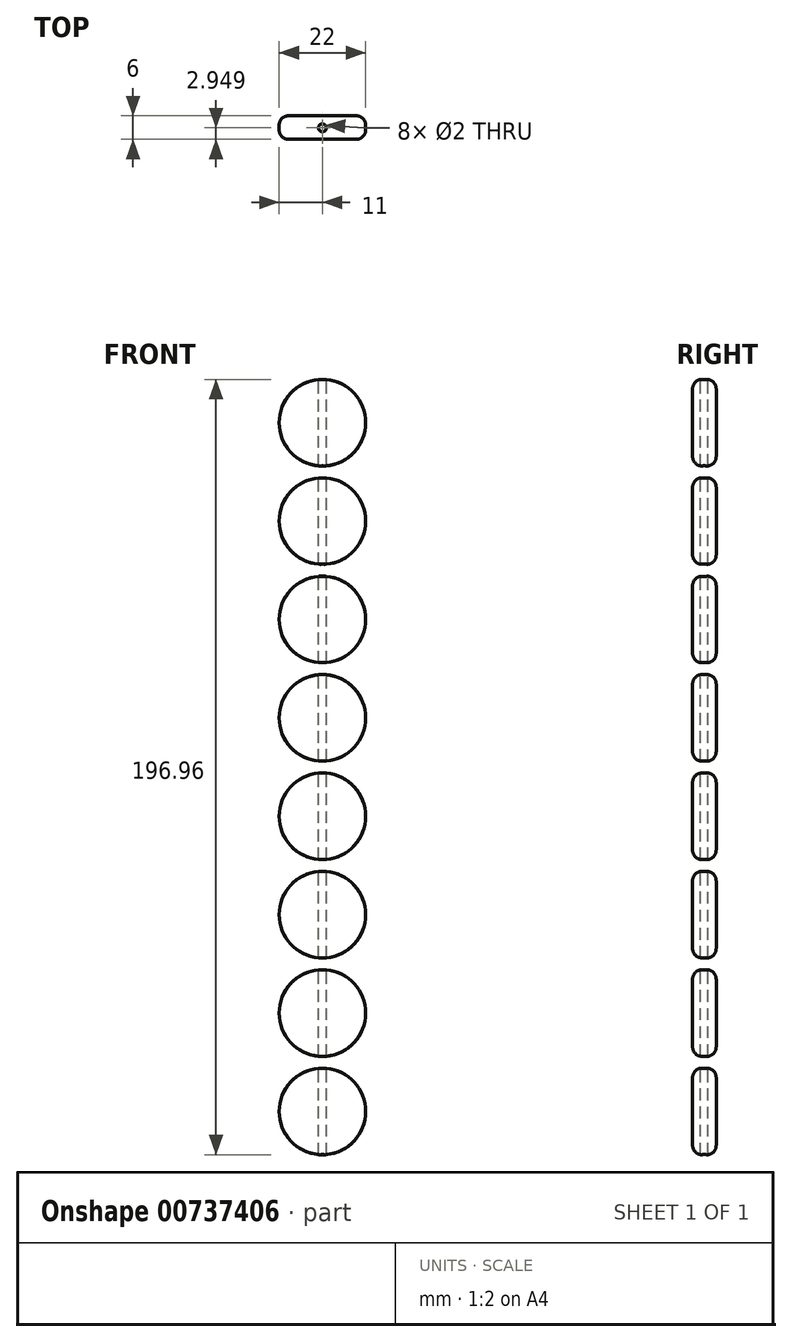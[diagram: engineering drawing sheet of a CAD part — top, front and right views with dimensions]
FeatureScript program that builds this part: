
annotation { "Feature Type Name" : "Feature", "Feature Type Description" : "" }
export const myFeature = defineFeature(function(context is Context, id is Id, definition is map)
    precondition{}
    {
        {
            var Q0;
            Q0=qCreatedBy(makeId("Front.planeOp"),FACE);
            var sketch = newSketch(context, id + "F0", { "sketchPlane" : qUnion([Q0])});
            skCircle(sketch, "E0", {"center": v(0, 0) * mm, "radius": 11 * mm});
            skCircle(sketch, "E1.0.1.0", {"center": v(0, -25) * mm, "radius": 11 * mm});
            skCircle(sketch, "E1.0.2.0", {"center": v(0, -50) * mm, "radius": 11 * mm});
            skCircle(sketch, "E1.0.3.0", {"center": v(0, -75) * mm, "radius": 11 * mm});
            skCircle(sketch, "E1.0.4.0", {"center": v(0, -100) * mm, "radius": 11 * mm});
            skCircle(sketch, "E1.0.5.0", {"center": v(0, -125) * mm, "radius": 11 * mm});
            skCircle(sketch, "E1.0.6.0", {"center": v(0, -150) * mm, "radius": 11 * mm});
            skCircle(sketch, "E1.0.7.0", {"center": v(0, -175) * mm, "radius": 11 * mm});
            skLineSegment(sketch, "E1.direction1", {"start": v(0, 0) * mm, "end": v(25, 0) * mm, "construction": true});
            skLineSegment(sketch, "E1.direction2", {"start": v(0, 0) * mm, "end": v(0, -25) * mm, "construction": true});
            skLineSegment(sketch, "E2", {"start": v(0, 0) * mm, "end": v(0, -175) * mm, "construction": true});
            skSolve(sketch);
        }
        {
            var Q0;
            Q0 = qSketchRegion(id + "F0", true);
            extrude(context, id + "F1", {"entities" : qUnion([Q0]), "depth" : 6 * mm, "offsetDistance" : 25 * mm});
        }
        {
            var Q0;
            Q0=makeQuery(id+"F1.opExtrude","CAP_EDGE",EDGE,{"disambiguationData":[OSD([sQuery(id+"F0.wireOp",EDGE,"E0")])],"isStart":true});
            var Q1;
            Q1=makeQuery(id+"F1.opExtrude","CAP_EDGE",EDGE,{"disambiguationData":[OSD([sQuery(id+"F0.wireOp",EDGE,"E0")])],"isStart":false});
            var Q2;
            Q2=makeQuery(id+"F1.opExtrude","CAP_FACE",FACE,{"disambiguationData":[OSD([sQuery(id+"F0.wireOp",EDGE,"E1.0.1.0")])],"isStart":false});
            var Q3;
            Q3=makeQuery(id+"F1.opExtrude","CAP_FACE",FACE,{"disambiguationData":[OSD([sQuery(id+"F0.wireOp",EDGE,"E1.0.2.0")])],"isStart":false});
            var Q4;
            Q4=makeQuery(id+"F1.opExtrude","CAP_FACE",FACE,{"disambiguationData":[OSD([sQuery(id+"F0.wireOp",EDGE,"E1.0.3.0")])],"isStart":false});
            var Q5;
            Q5=makeQuery(id+"F1.opExtrude","CAP_FACE",FACE,{"disambiguationData":[OSD([sQuery(id+"F0.wireOp",EDGE,"E1.0.4.0")])],"isStart":false});
            var Q6;
            Q6=makeQuery(id+"F1.opExtrude","CAP_FACE",FACE,{"disambiguationData":[OSD([sQuery(id+"F0.wireOp",EDGE,"E1.0.5.0")])],"isStart":false});
            var Q7;
            Q7=makeQuery(id+"F1.opExtrude","CAP_FACE",FACE,{"disambiguationData":[OSD([sQuery(id+"F0.wireOp",EDGE,"E1.0.6.0")])],"isStart":false});
            var Q8;
            Q8=makeQuery(id+"F1.opExtrude","CAP_FACE",FACE,{"disambiguationData":[OSD([sQuery(id+"F0.wireOp",EDGE,"E1.0.7.0")])],"isStart":false});
            var Q9;
            Q9=makeQuery(id+"F1.opExtrude","CAP_FACE",FACE,{"disambiguationData":[OSD([sQuery(id+"F0.wireOp",EDGE,"E1.0.1.0")])],"isStart":true});
            var Q10;
            Q10=makeQuery(id+"F1.opExtrude","CAP_FACE",FACE,{"disambiguationData":[OSD([sQuery(id+"F0.wireOp",EDGE,"E1.0.2.0")])],"isStart":true});
            var Q11;
            Q11=makeQuery(id+"F1.opExtrude","CAP_FACE",FACE,{"disambiguationData":[OSD([sQuery(id+"F0.wireOp",EDGE,"E1.0.3.0")])],"isStart":true});
            var Q12;
            Q12=makeQuery(id+"F1.opExtrude","CAP_FACE",FACE,{"disambiguationData":[OSD([sQuery(id+"F0.wireOp",EDGE,"E1.0.4.0")])],"isStart":true});
            var Q13;
            Q13=makeQuery(id+"F1.opExtrude","CAP_FACE",FACE,{"disambiguationData":[OSD([sQuery(id+"F0.wireOp",EDGE,"E1.0.5.0")])],"isStart":true});
            var Q14;
            Q14=makeQuery(id+"F1.opExtrude","CAP_FACE",FACE,{"disambiguationData":[OSD([sQuery(id+"F0.wireOp",EDGE,"E1.0.6.0")])],"isStart":true});
            var Q15;
            Q15=makeQuery(id+"F1.opExtrude","CAP_FACE",FACE,{"disambiguationData":[OSD([sQuery(id+"F0.wireOp",EDGE,"E1.0.7.0")])],"isStart":true});
            fillet(context, id + "F2", {"entities" : qUnion([Q0, Q1, Q2, Q3, Q4, Q5, Q6, Q7, Q8, Q9, Q10, Q11, Q12, Q13, Q14, Q15]), "radius" : 2.4 * mm, "tangentPropagation" : true, "allowEdgeOverflow" : false});
        }
        {
            var Q0;
            Q0=qCreatedBy(makeId("Top.planeOp"),FACE);
            var sketch = newSketch(context, id + "F3", { "sketchPlane" : qUnion([Q0])});
            skLineSegment(sketch, "E3", {"start": v(-10.99, -3.05) * mm, "end": v(8, -3.05) * mm, "construction": true});
            skLineSegment(sketch, "E4", {"start": v(8, -3.05) * mm, "end": v(0, -3.05) * mm, "construction": true});
            skLineSegment(sketch, "E5", {"start": v(0, -3.05) * mm, "end": v(0, 0) * mm});
            skCircle(sketch, "E6", {"center": v(0, -3.05) * mm, "radius": 1 * mm});
            skSolve(sketch);
        }
        {
            var Q0;
            Q0 = qSketchRegion(id + "F3", true);
            var Q1;
            Q1=sQuery(id+"F3.wireOp",EDGE,"E6");
            extrude(context, id + "F4", {"entities" : qUnion([Q0]), "operationType" : NewBodyOperationType.REMOVE, "surfaceEntities" : qUnion([Q1]), "endBound" : BoundingType.THROUGH_ALL, "oppositeDirection" : true, "depth" : 25 * mm, "offsetDistance" : 25 * mm, "hasSecondDirection" : true, "secondDirectionBound" : SecondDirectionBoundingType.THROUGH_ALL, "secondDirectionOppositeDirection" : false, "secondDirectionDepth" : 25 * mm});
        }
    });
